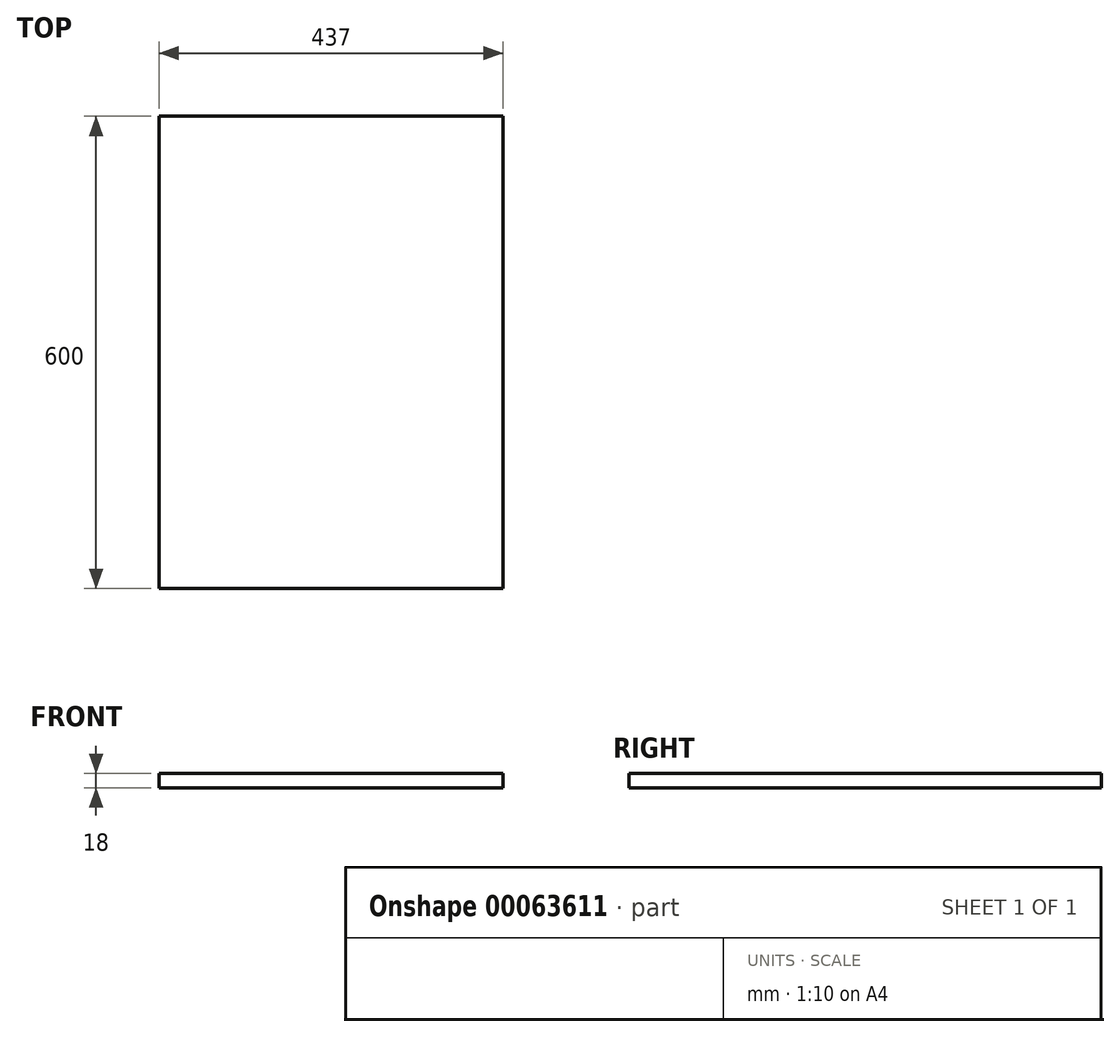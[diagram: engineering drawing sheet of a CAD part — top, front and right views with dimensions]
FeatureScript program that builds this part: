
annotation { "Feature Type Name" : "Feature", "Feature Type Description" : "" }
export const myFeature = defineFeature(function(context is Context, id is Id, definition is map)
    precondition{}
    {
        {
            var Q0;
            Q0=qCreatedBy(makeId("Top.planeOp"),FACE);
            var sketch = newSketch(context, id + "F0", { "sketchPlane" : qUnion([Q0])});
            skLineSegment(sketch, "E0.bottom", {"start": v(0, 0) * mm, "end": v(437, 0) * mm});
            skLineSegment(sketch, "E0.top", {"start": v(0, -600) * mm, "end": v(437, -600) * mm});
            skLineSegment(sketch, "E0.left", {"start": v(0, 0) * mm, "end": v(0, -600) * mm});
            skLineSegment(sketch, "E0.right", {"start": v(437, 0) * mm, "end": v(437, -600) * mm});
            skSolve(sketch);
        }
        {
            var Q0;
            Q0=makeQuery(id+"F0.imprint","IMPRINT",FACE,{"disambiguationData":[TD([[makeQuery(id+"F0.imprint","IMPRINT",EDGE,{"derivedFrom":sQuery(id+"F0.wireOp",EDGE,"E0.bottom")}),-1.0]])]});
            extrude(context, id + "F1", {"entities" : qUnion([Q0]), "depth" : 18 * mm});
        }
    });
